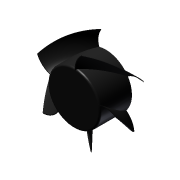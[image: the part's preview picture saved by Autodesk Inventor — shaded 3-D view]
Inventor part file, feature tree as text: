
AUTODESK INVENTOR PART (.ipt)
format: ipt  version: 2014 SP1 (Build 180222100, 222)  size: 239,616 bytes
history: native  units: mm (DEFAULTED — no unit token found)
features: sketch x2, extrude x1, fillet x1, other x1, helix x1, pattern_circular x1
ambient origin geometry x8: Origin, YZ Plane, XZ Plane, XY Plane, X Axis, Y Axis, Z Axis, Center Point
bodies: Solid1 (feature_tree)
feature tree (7):
  extrude  "Extrusion1"  Depth=0.79375mm
  fillet  "Fillet1"  Radius=0.3175mm
  sketch  "Sketch2"  dims[d5=0.698132mm d6=8.89mm d7=37.338mm d8=127.0mm d9=14.3002mm d10=1.5mm d11=0.0mm d12=90.0deg d13=90.0deg d14=0.0mm d15=0.0mm d16=50.0mm d18=360.0deg]
  other  "Work Axis1"
  helix  "Coil1"  [1 undecoded]
  pattern_circular  "Circular Pattern1"  [2 undecoded]
  sketch  "Sketch1"  dims[d0=14.3002mm d1=0.0mm d2=0.79375mm d3=0.3175mm d4=2.094086mm]
note: 3 required parameter values undecoded (feature->parameter linkage not recoverable at this tier; creation-order binding heuristic only, values carry confidence <= 0.55)
